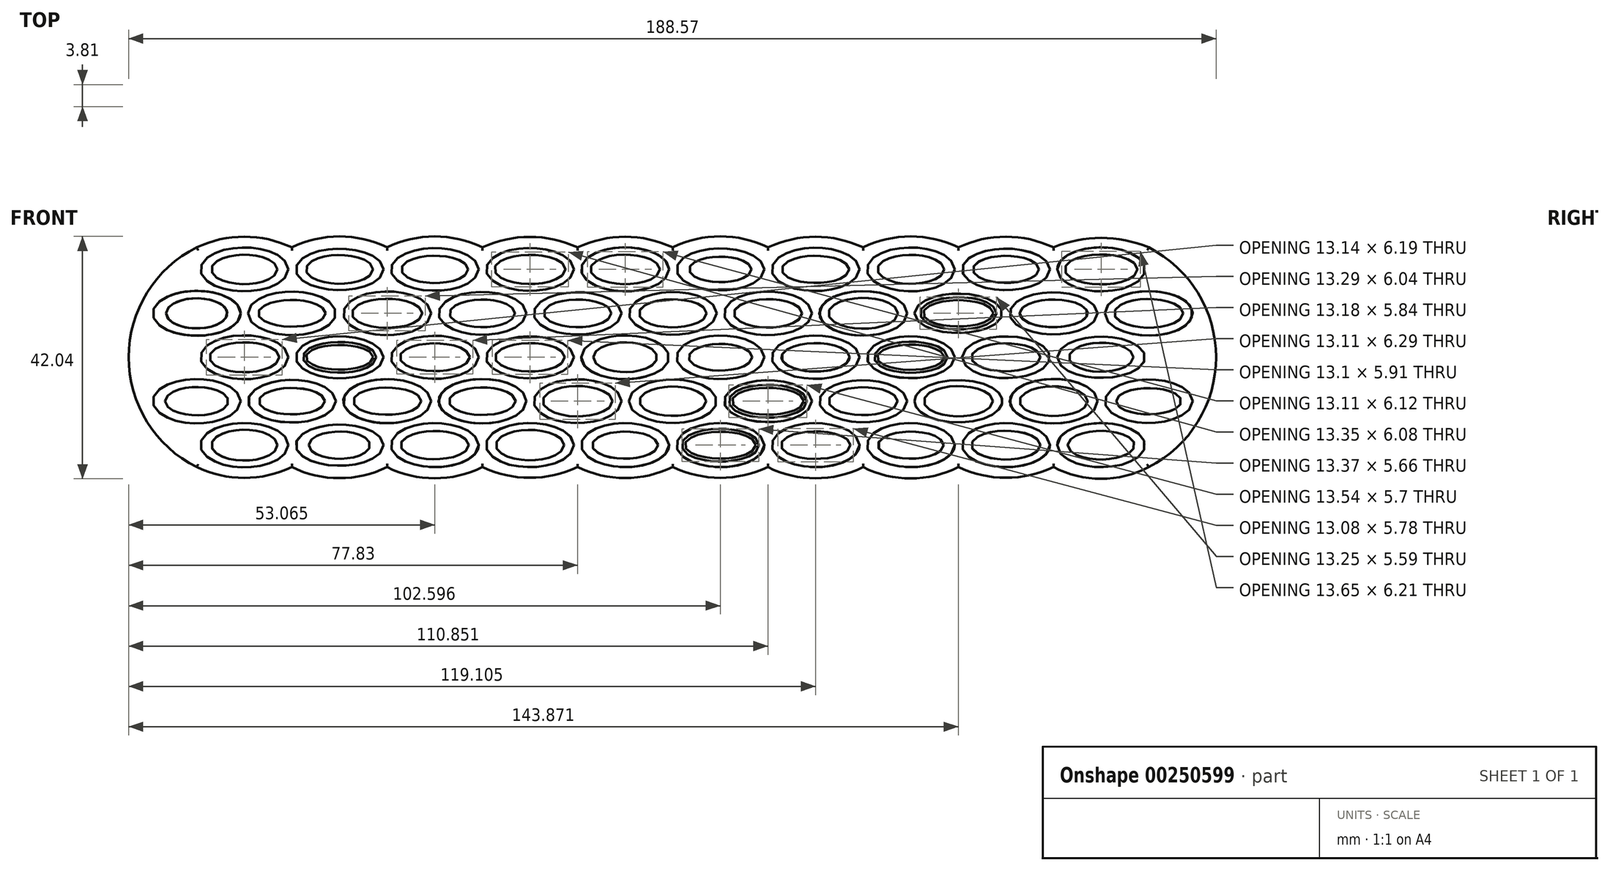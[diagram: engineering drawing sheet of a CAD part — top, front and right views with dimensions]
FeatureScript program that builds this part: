
annotation { "Feature Type Name" : "Feature", "Feature Type Description" : "" }
export const myFeature = defineFeature(function(context is Context, id is Id, definition is map)
    precondition{}
    {
        {
            var Q0;
            Q0=qCreatedBy(makeId("Front.planeOp"),FACE);
            var sketch = newSketch(context, id + "F3", { "sketchPlane" : qUnion([Q0])});
            skPoint(sketch, "E0.middle", {"position": v(0, 0) * mm});
            skEllipse(sketch, "E1", {"center": v(-74.3, 15.24) * mm, "majorRadius": 7.62 * mm, "minorRadius": 3.8 * mm, "majorAxis": v(1, 0)});
            skEllipse(sketch, "E2", {"center": v(-66.04, 7.62) * mm, "majorRadius": 7.62 * mm, "minorRadius": 3.76 * mm, "majorAxis": v(-1, 0)});
            skEllipse(sketch, "E3", {"center": v(-57.79, 15.24) * mm, "majorRadius": 7.62 * mm, "minorRadius": 3.58 * mm, "majorAxis": v(1, 0)});
            skEllipse(sketch, "E4", {"center": v(-66.04, -7.62) * mm, "majorRadius": 7.62 * mm, "minorRadius": 3.7 * mm, "majorAxis": v(1, 0)});
            skEllipse(sketch, "E5", {"center": v(-74.3, -15.24) * mm, "majorRadius": 7.62 * mm, "minorRadius": 3.84 * mm, "majorAxis": v(1, 0)});
            skEllipse(sketch, "E6", {"center": v(-57.79, -15.24) * mm, "majorRadius": 7.62 * mm, "minorRadius": 3.55 * mm, "majorAxis": v(1, 0)});
            skEllipse(sketch, "E7", {"center": v(-74.3, 0) * mm, "majorRadius": 7.62 * mm, "minorRadius": 3.8 * mm, "majorAxis": v(1, 0)});
            skEllipse(sketch, "E8", {"center": v(-57.79, 0) * mm, "majorRadius": 7.62 * mm, "minorRadius": 3.63 * mm, "majorAxis": v(1, 0)});
            skEllipse(sketch, "E9", {"center": v(-49.53, 7.62) * mm, "majorRadius": 7.62 * mm, "minorRadius": 3.79 * mm, "majorAxis": v(1, 0)});
            skEllipse(sketch, "E10", {"center": v(-49.53, -7.62) * mm, "majorRadius": 7.62 * mm, "minorRadius": 3.81 * mm, "majorAxis": v(1, 0)});
            skEllipse(sketch, "E11", {"center": v(-41.28, 15.24) * mm, "majorRadius": 7.62 * mm, "minorRadius": 3.7 * mm, "majorAxis": v(1, 0)});
            skEllipse(sketch, "E12", {"center": v(-41.28, 0) * mm, "majorRadius": 7.62 * mm, "minorRadius": 3.73 * mm, "majorAxis": v(1, 0)});
            skEllipse(sketch, "E13", {"center": v(-41.27, -15.24) * mm, "majorRadius": 7.62 * mm, "minorRadius": 3.81 * mm, "majorAxis": v(1, 0)});
            skEllipse(sketch, "E14", {"center": v(-33.02, 7.62) * mm, "majorRadius": 7.62 * mm, "minorRadius": 3.72 * mm, "majorAxis": v(1, 0)});
            skEllipse(sketch, "E15", {"center": v(-33.02, -7.62) * mm, "majorRadius": 7.62 * mm, "minorRadius": 3.85 * mm, "majorAxis": v(1, 0)});
            skEllipse(sketch, "E16", {"center": v(-24.77, 15.24) * mm, "majorRadius": 7.62 * mm, "minorRadius": 3.72 * mm, "majorAxis": v(1, 0)});
            skEllipse(sketch, "E17", {"center": v(-24.77, 0) * mm, "majorRadius": 7.62 * mm, "minorRadius": 3.64 * mm, "majorAxis": v(1, 0)});
            skEllipse(sketch, "E18", {"center": v(-24.77, -15.24) * mm, "majorRadius": 7.62 * mm, "minorRadius": 3.82 * mm, "majorAxis": v(1, 0)});
            skEllipse(sketch, "E19", {"center": v(-16.51, 7.62) * mm, "majorRadius": 7.62 * mm, "minorRadius": 3.67 * mm, "majorAxis": v(1, 0)});
            skEllipse(sketch, "E20", {"center": v(-16.51, -7.62) * mm, "majorRadius": 7.62 * mm, "minorRadius": 3.8 * mm, "majorAxis": v(1, 0)});
            skEllipse(sketch, "E21", {"center": v(-8.26, 15.24) * mm, "majorRadius": 7.62 * mm, "minorRadius": 3.81 * mm, "majorAxis": v(1, 0)});
            skEllipse(sketch, "E22", {"center": v(-8.25, -15.24) * mm, "majorRadius": 7.62 * mm, "minorRadius": 3.81 * mm, "majorAxis": v(1, 0)});
            skEllipse(sketch, "E23", {"center": v(-8.26, 0) * mm, "majorRadius": 7.62 * mm, "minorRadius": 3.8 * mm, "majorAxis": v(-1, 0)});
            skEllipse(sketch, "E24", {"center": v(0, 7.62) * mm, "majorRadius": 7.62 * mm, "minorRadius": 3.7 * mm, "majorAxis": v(1, 0)});
            skEllipse(sketch, "E25", {"center": v(0, -7.62) * mm, "majorRadius": 7.62 * mm, "minorRadius": 3.77 * mm, "majorAxis": v(-1, 0)});
            skEllipse(sketch, "E26", {"center": v(8.26, 15.24) * mm, "majorRadius": 7.62 * mm, "minorRadius": 3.63 * mm, "majorAxis": v(1, 0)});
            skEllipse(sketch, "E27", {"center": v(8.26, 0) * mm, "majorRadius": 7.62 * mm, "minorRadius": 3.78 * mm, "majorAxis": v(1, 0)});
            skEllipse(sketch, "E28", {"center": v(8.26, -15.24) * mm, "majorRadius": 7.62 * mm, "minorRadius": 3.81 * mm, "majorAxis": v(1, 0)});
            skEllipse(sketch, "E29", {"center": v(16.51, 7.62) * mm, "majorRadius": 7.62 * mm, "minorRadius": 3.79 * mm, "majorAxis": v(1, 0)});
            skEllipse(sketch, "E30", {"center": v(24.77, 15.24) * mm, "majorRadius": 7.62 * mm, "minorRadius": 3.75 * mm, "majorAxis": v(1, 0)});
            skEllipse(sketch, "E31", {"center": v(24.77, 0) * mm, "majorRadius": 7.62 * mm, "minorRadius": 3.75 * mm, "majorAxis": v(1, 0)});
            skEllipse(sketch, "E32", {"center": v(16.51, -7.62) * mm, "majorRadius": 7.62 * mm, "minorRadius": 3.62 * mm, "majorAxis": v(1, 0)});
            skEllipse(sketch, "E33", {"center": v(24.77, -15.24) * mm, "majorRadius": 7.62 * mm, "minorRadius": 3.81 * mm, "majorAxis": v(1, 0)});
            skEllipse(sketch, "E34", {"center": v(33.02, -7.62) * mm, "majorRadius": 7.62 * mm, "minorRadius": 3.65 * mm, "majorAxis": v(1, 0)});
            skEllipse(sketch, "E35", {"center": v(41.28, -15.24) * mm, "majorRadius": 7.62 * mm, "minorRadius": 3.81 * mm, "majorAxis": v(1, 0)});
            skEllipse(sketch, "E36", {"center": v(41.28, 0) * mm, "majorRadius": 7.62 * mm, "minorRadius": 3.62 * mm, "majorAxis": v(1, 0)});
            skEllipse(sketch, "E37", {"center": v(33.02, 7.62) * mm, "majorRadius": 7.62 * mm, "minorRadius": 3.85 * mm, "majorAxis": v(1, 0)});
            skEllipse(sketch, "E38", {"center": v(41.28, 15.24) * mm, "majorRadius": 7.62 * mm, "minorRadius": 3.8 * mm, "majorAxis": v(1, 0)});
            skEllipse(sketch, "E39", {"center": v(49.53, 7.62) * mm, "majorRadius": 7.62 * mm, "minorRadius": 3.41 * mm, "majorAxis": v(-1, 0)});
            skEllipse(sketch, "E40", {"center": v(49.53, -7.62) * mm, "majorRadius": 7.62 * mm, "minorRadius": 3.68 * mm, "majorAxis": v(-1, 0)});
            skEllipse(sketch, "E41", {"center": v(57.79, -15.24) * mm, "majorRadius": 7.62 * mm, "minorRadius": 3.81 * mm, "majorAxis": v(1, 0)});
            skEllipse(sketch, "E42", {"center": v(57.79, 0) * mm, "majorRadius": 7.62 * mm, "minorRadius": 3.6 * mm, "majorAxis": v(-1, 0)});
            skEllipse(sketch, "E43", {"center": v(66.04, 7.62) * mm, "majorRadius": 7.62 * mm, "minorRadius": 3.66 * mm, "majorAxis": v(1, 0)});
            skEllipse(sketch, "E44", {"center": v(57.79, 15.24) * mm, "majorRadius": 7.62 * mm, "minorRadius": 3.6 * mm, "majorAxis": v(1, 0)});
            skPoint(sketch, "E44.centerSnap0", {"position": v(57.79, 3.6) * mm});
            skEllipse(sketch, "E45", {"center": v(66.04, -7.62) * mm, "majorRadius": 7.62 * mm, "minorRadius": 3.85 * mm, "majorAxis": v(1, 0)});
            skEllipse(sketch, "E46", {"center": v(74.3, 15.24) * mm, "majorRadius": 7.62 * mm, "minorRadius": 3.81 * mm, "majorAxis": v(-1, 0)});
            skEllipse(sketch, "E47", {"center": v(74.3, 0) * mm, "majorRadius": 7.62 * mm, "minorRadius": 3.57 * mm, "majorAxis": v(-1, 0)});
            skEllipse(sketch, "E48", {"center": v(74.3, -15.24) * mm, "majorRadius": 7.62 * mm, "minorRadius": 3.81 * mm, "majorAxis": v(-1, 0)});
            skPoint(sketch, "E49.endSnap0", {"position": v(-66.04, 3.86) * mm});
            skArc(sketch, "E50", {"start": v(-66.04, 19.05) * mm, "mid": v(-74.3, 20.91) * mm, "end": v(-82.55, 19.05) * mm});
            skArc(sketch, "E51", {"start": v(-49.53, 19.05) * mm, "mid": v(-57.79, 20.96) * mm, "end": v(-66.04, 19.05) * mm});
            skArc(sketch, "E52", {"start": v(-33.02, 19.05) * mm, "mid": v(-41.28, 20.96) * mm, "end": v(-49.53, 19.05) * mm});
            skArc(sketch, "E53", {"start": v(-16.51, 19.05) * mm, "mid": v(-24.77, 20.88) * mm, "end": v(-33.02, 19.05) * mm});
            skArc(sketch, "E54", {"start": v(0, 19.05) * mm, "mid": v(-8.26, 20.9) * mm, "end": v(-16.51, 19.05) * mm});
            skArc(sketch, "E55", {"start": v(16.51, 19.05) * mm, "mid": v(8.26, 20.97) * mm, "end": v(0, 19.05) * mm});
            skArc(sketch, "E56", {"start": v(33.02, 19.05) * mm, "mid": v(24.77, 20.9) * mm, "end": v(16.51, 19.05) * mm});
            skArc(sketch, "E57", {"start": v(49.53, 19.05) * mm, "mid": v(41.28, 20.96) * mm, "end": v(33.02, 19.05) * mm});
            skArc(sketch, "E58", {"start": v(66.04, 19.05) * mm, "mid": v(57.79, 20.9) * mm, "end": v(49.53, 19.05) * mm});
            skArc(sketch, "E59", {"start": v(82.55, 19.05) * mm, "mid": v(74.3, 20.7) * mm, "end": v(66.04, 19.05) * mm});
            skPoint(sketch, "E60.endSnap0", {"position": v(81.92, 0) * mm});
            skArc(sketch, "E61", {"start": v(-82.55, -19.05) * mm, "mid": v(-74.3, -20.92) * mm, "end": v(-66.04, -19.05) * mm});
            skArc(sketch, "E62", {"start": v(-66.04, -19.05) * mm, "mid": v(-57.79, -20.96) * mm, "end": v(-49.53, -19.05) * mm});
            skArc(sketch, "E63", {"start": v(-49.53, -19.05) * mm, "mid": v(-41.28, -20.99) * mm, "end": v(-33.02, -19.05) * mm});
            skArc(sketch, "E64", {"start": v(-33.02, -19.05) * mm, "mid": v(-24.77, -20.9) * mm, "end": v(-16.51, -19.05) * mm});
            skArc(sketch, "E65", {"start": v(-16.5, -19.05) * mm, "mid": v(-8.25, -20.94) * mm, "end": v(0, -19.05) * mm});
            skArc(sketch, "E66", {"start": v(0, -19.05) * mm, "mid": v(8.26, -20.9) * mm, "end": v(16.51, -19.05) * mm});
            skArc(sketch, "E67", {"start": v(16.51, -19.05) * mm, "mid": v(24.77, -21) * mm, "end": v(33.02, -19.05) * mm});
            skArc(sketch, "E68", {"start": v(33.02, -19.05) * mm, "mid": v(41.28, -21.02) * mm, "end": v(49.53, -19.05) * mm});
            skArc(sketch, "E69", {"start": v(49.53, -19.05) * mm, "mid": v(57.79, -20.9) * mm, "end": v(66.04, -19.05) * mm});
            skArc(sketch, "E70", {"start": v(66.04, -19.05) * mm, "mid": v(74.3, -21.07) * mm, "end": v(82.55, -19.05) * mm});
            skArc(sketch, "E71", {"start": v(82.55, -19.05) * mm, "mid": v(94.23, 0) * mm, "end": v(82.55, 19.05) * mm});
            skPoint(sketch, "E72.endSnap0", {"position": v(73.66, -7.62) * mm});
            skEllipse(sketch, "E73", {"center": v(82.55, 7.62) * mm, "majorRadius": 7.62 * mm, "minorRadius": 3.85 * mm, "majorAxis": v(-1, 0)});
            skEllipse(sketch, "E74", {"center": v(82.55, -7.62) * mm, "majorRadius": 7.62 * mm, "minorRadius": 3.76 * mm, "majorAxis": v(1, 0)});
            skArc(sketch, "E75", {"start": v(-82.55, 19.05) * mm, "mid": v(-94.34, 0) * mm, "end": v(-82.55, -19.05) * mm});
            skEllipse(sketch, "E76", {"center": v(-82.55, 7.62) * mm, "majorRadius": 7.62 * mm, "minorRadius": 3.88 * mm, "majorAxis": v(1, 0)});
            skPoint(sketch, "E76.centerSnap0", {"position": v(-77.03, 7.62) * mm});
            skEllipse(sketch, "E77", {"center": v(-82.55, -7.62) * mm, "majorRadius": 7.62 * mm, "minorRadius": 3.83 * mm, "majorAxis": v(1, 0)});
            skEllipse(sketch, "E78", {"center": v(74.3, 15.24) * mm, "majorRadius": 6.32 * mm, "minorRadius": 2.6 * mm, "majorAxis": v(1, 0)});
            skEllipse(sketch, "E79", {"center": v(82.55, 7.62) * mm, "majorRadius": 5.98 * mm, "minorRadius": 2.5 * mm, "majorAxis": v(1, 0)});
            skEllipse(sketch, "E80", {"center": v(74.3, 0) * mm, "majorRadius": 5.58 * mm, "minorRadius": 2.51 * mm, "majorAxis": v(1, 0)});
            skEllipse(sketch, "E81", {"center": v(82.55, -7.62) * mm, "majorRadius": 5.66 * mm, "minorRadius": 2.27 * mm, "majorAxis": v(-1, 0)});
            skEllipse(sketch, "E82", {"center": v(57.79, 15.24) * mm, "majorRadius": 5.74 * mm, "minorRadius": 2.35 * mm, "majorAxis": v(1, 0)});
            skEllipse(sketch, "E83", {"center": v(66.04, 7.62) * mm, "majorRadius": 5.9 * mm, "minorRadius": 2.38 * mm, "majorAxis": v(-1, 0)});
            skEllipse(sketch, "E84", {"center": v(74.3, -15.24) * mm, "majorRadius": 5.8 * mm, "minorRadius": 2.49 * mm, "majorAxis": v(-1, 0)});
            skEllipse(sketch, "E85", {"center": v(66.04, -7.62) * mm, "majorRadius": 5.93 * mm, "minorRadius": 2.57 * mm, "majorAxis": v(1, 0)});
            skEllipse(sketch, "E86", {"center": v(57.79, -15.24) * mm, "majorRadius": 5.97 * mm, "minorRadius": 2.5 * mm, "majorAxis": v(1, 0)});
            skEllipse(sketch, "E87", {"center": v(57.79, 0) * mm, "majorRadius": 6 * mm, "minorRadius": 2.43 * mm, "majorAxis": v(1, 0)});
            skEllipse(sketch, "E88", {"center": v(49.53, 7.62) * mm, "majorRadius": 6.12 * mm, "minorRadius": 2.29 * mm, "majorAxis": v(1, 0)});
            skEllipse(sketch, "E89", {"center": v(41.28, 15.24) * mm, "majorRadius": 5.78 * mm, "minorRadius": 2.5 * mm, "majorAxis": v(1, 0)});
            skEllipse(sketch, "E90", {"center": v(33.02, 7.62) * mm, "majorRadius": 6.02 * mm, "minorRadius": 2.67 * mm, "majorAxis": v(1, 0)});
            skEllipse(sketch, "E91", {"center": v(24.77, 15.24) * mm, "majorRadius": 5.85 * mm, "minorRadius": 2.36 * mm, "majorAxis": v(1, 0)});
            skEllipse(sketch, "E92", {"center": v(8.26, 15.24) * mm, "majorRadius": 5.43 * mm, "minorRadius": 2.2 * mm, "majorAxis": v(1, 0)});
            skEllipse(sketch, "E93", {"center": v(16.51, 7.62) * mm, "majorRadius": 5.93 * mm, "minorRadius": 2.46 * mm, "majorAxis": v(1, 0)});
            skEllipse(sketch, "E94", {"center": v(24.77, 0) * mm, "majorRadius": 5.93 * mm, "minorRadius": 2.47 * mm, "majorAxis": v(1, 0)});
            skEllipse(sketch, "E95", {"center": v(41.28, 0) * mm, "majorRadius": 5.84 * mm, "minorRadius": 2.19 * mm, "majorAxis": v(1, 0)});
            skEllipse(sketch, "E96", {"center": v(49.53, -7.62) * mm, "majorRadius": 5.98 * mm, "minorRadius": 2.63 * mm, "majorAxis": v(1, 0)});
            skEllipse(sketch, "E97", {"center": v(33.02, -7.62) * mm, "majorRadius": 6 * mm, "minorRadius": 2.41 * mm, "majorAxis": v(1, 0)});
            skEllipse(sketch, "E98", {"center": v(41.28, -15.24) * mm, "majorRadius": 5.7 * mm, "minorRadius": 2.35 * mm, "majorAxis": v(1, 0)});
            skEllipse(sketch, "E99", {"center": v(24.77, -15.24) * mm, "majorRadius": 6.03 * mm, "minorRadius": 2.38 * mm, "majorAxis": v(1, 0)});
            skEllipse(sketch, "E100", {"center": v(16.51, -7.62) * mm, "majorRadius": 6.26 * mm, "minorRadius": 2.34 * mm, "majorAxis": v(1, 0)});
            skEllipse(sketch, "E101", {"center": v(8.26, -15.24) * mm, "majorRadius": 6.18 * mm, "minorRadius": 2.32 * mm, "majorAxis": v(1, 0)});
            skEllipse(sketch, "E102", {"center": v(0, 7.62) * mm, "majorRadius": 5.88 * mm, "minorRadius": 2.43 * mm, "majorAxis": v(1, 0)});
            skEllipse(sketch, "E103", {"center": v(8.26, 0) * mm, "majorRadius": 5.5 * mm, "minorRadius": 2.3 * mm, "majorAxis": v(1, 0)});
            skEllipse(sketch, "E104", {"center": v(0, -7.62) * mm, "majorRadius": 5.79 * mm, "minorRadius": 2.54 * mm, "majorAxis": v(1, 0)});
            skEllipse(sketch, "E105", {"center": v(-8.26, 0) * mm, "majorRadius": 5.54 * mm, "minorRadius": 2.57 * mm, "majorAxis": v(-1, 0)});
            skEllipse(sketch, "E106", {"center": v(-24.77, 15.24) * mm, "majorRadius": 6.16 * mm, "minorRadius": 2.53 * mm, "majorAxis": v(1, 0)});
            skEllipse(sketch, "E107", {"center": v(-8.26, 15.24) * mm, "majorRadius": 6.05 * mm, "minorRadius": 2.55 * mm, "majorAxis": v(1, 0)});
            skEllipse(sketch, "E108", {"center": v(-16.51, 7.62) * mm, "majorRadius": 5.88 * mm, "minorRadius": 2.4 * mm, "majorAxis": v(1, 0)});
            skEllipse(sketch, "E109", {"center": v(-41.28, 15.24) * mm, "majorRadius": 5.8 * mm, "minorRadius": 2.37 * mm, "majorAxis": v(1, 0)});
            skEllipse(sketch, "E110", {"center": v(-33.02, 7.62) * mm, "majorRadius": 5.7 * mm, "minorRadius": 2.39 * mm, "majorAxis": v(1, 0)});
            skEllipse(sketch, "E111", {"center": v(-24.77, 0) * mm, "majorRadius": 6.04 * mm, "minorRadius": 2.45 * mm, "majorAxis": v(1, 0)});
            skEllipse(sketch, "E112", {"center": v(-16.51, -7.62) * mm, "majorRadius": 6.05 * mm, "minorRadius": 2.64 * mm, "majorAxis": v(1, 0)});
            skEllipse(sketch, "E113", {"center": v(-8.25, -15.24) * mm, "majorRadius": 5.72 * mm, "minorRadius": 2.35 * mm, "majorAxis": v(1, 0)});
            skEllipse(sketch, "E114", {"center": v(-24.77, -15.24) * mm, "majorRadius": 5.94 * mm, "minorRadius": 2.63 * mm, "majorAxis": v(1, 0)});
            skEllipse(sketch, "E115", {"center": v(-41.27, -15.24) * mm, "majorRadius": 5.92 * mm, "minorRadius": 2.44 * mm, "majorAxis": v(1, 0)});
            skEllipse(sketch, "E116", {"center": v(-33.02, -7.62) * mm, "majorRadius": 5.8 * mm, "minorRadius": 2.38 * mm, "majorAxis": v(1, 0)});
            skEllipse(sketch, "E117", {"center": v(-41.28, 0) * mm, "majorRadius": 6.08 * mm, "minorRadius": 2.41 * mm, "majorAxis": v(1, 0)});
            skEllipse(sketch, "E118", {"center": v(-49.53, 7.62) * mm, "majorRadius": 6.14 * mm, "minorRadius": 2.51 * mm, "majorAxis": v(1, 0)});
            skEllipse(sketch, "E119", {"center": v(-57.79, 15.24) * mm, "majorRadius": 5.81 * mm, "minorRadius": 2.5 * mm, "majorAxis": v(1, 0)});
            skEllipse(sketch, "E120", {"center": v(-66.04, 7.62) * mm, "majorRadius": 5.84 * mm, "minorRadius": 2.32 * mm, "majorAxis": v(1, 0)});
            skEllipse(sketch, "E121", {"center": v(-74.3, 15.24) * mm, "majorRadius": 5.74 * mm, "minorRadius": 2.55 * mm, "majorAxis": v(1, 0)});
            skEllipse(sketch, "E122", {"center": v(-82.55, 7.62) * mm, "majorRadius": 5.32 * mm, "minorRadius": 2.6 * mm, "majorAxis": v(-1, 0)});
            skEllipse(sketch, "E123", {"center": v(-74.3, 0) * mm, "majorRadius": 6.06 * mm, "minorRadius": 2.58 * mm, "majorAxis": v(1, 0)});
            skEllipse(sketch, "E124", {"center": v(-82.55, -7.62) * mm, "majorRadius": 5.5 * mm, "minorRadius": 2.44 * mm, "majorAxis": v(-1, 0)});
            skEllipse(sketch, "E125", {"center": v(-74.3, -15.24) * mm, "majorRadius": 5.74 * mm, "minorRadius": 2.68 * mm, "majorAxis": v(1, 0)});
            skEllipse(sketch, "E126", {"center": v(-57.79, -15.24) * mm, "majorRadius": 5.3 * mm, "minorRadius": 2.37 * mm, "majorAxis": v(-1, 0)});
            skEllipse(sketch, "E127", {"center": v(-66.04, -7.62) * mm, "majorRadius": 5.74 * mm, "minorRadius": 2.3 * mm, "majorAxis": v(1, 0)});
            skEllipse(sketch, "E128", {"center": v(-57.79, 0) * mm, "majorRadius": 5.85 * mm, "minorRadius": 2.13 * mm, "majorAxis": v(1, 0)});
            skEllipse(sketch, "E129", {"center": v(-49.53, -7.62) * mm, "majorRadius": 5.9 * mm, "minorRadius": 2.36 * mm, "majorAxis": v(1, 0)});
            skSolve(sketch);
        }
        {
            var Q0;
            Q0=makeQuery(id+"F3.imprint","IMPRINT",FACE,{"disambiguationData":[TD([[makeQuery(id+"F3.imprint","IMPRINT",EDGE,{"derivedFrom":sQuery(id+"F3.wireOp",EDGE,"E1")}),-1.0]])]});
            extrude(context, id + "F0", {"entities" : qUnion([Q0]), "depth" : 2.54 * mm});
        }
        {
            var Q0;
            Q0=makeQuery(id+"F3.imprint","IMPRINT",FACE,{"disambiguationData":[TD([[makeQuery(id+"F3.imprint","IMPRINT",EDGE,{"derivedFrom":sQuery(id+"F3.wireOp",EDGE,"E1")}),1.0]])]});
            var Q1;
            Q1=makeQuery(id+"F3.imprint","IMPRINT",FACE,{"disambiguationData":[TD([[makeQuery(id+"F3.imprint","IMPRINT",EDGE,{"derivedFrom":sQuery(id+"F3.wireOp",EDGE,"E76")}),1.0]])]});
            var Q2;
            Q2=makeQuery(id+"F3.imprint","IMPRINT",FACE,{"disambiguationData":[TD([[makeQuery(id+"F3.imprint","IMPRINT",EDGE,{"derivedFrom":sQuery(id+"F3.wireOp",EDGE,"E7")}),1.0]])]});
            var Q3;
            Q3=makeQuery(id+"F3.imprint","IMPRINT",FACE,{"disambiguationData":[TD([[makeQuery(id+"F3.imprint","IMPRINT",EDGE,{"derivedFrom":sQuery(id+"F3.wireOp",EDGE,"E77")}),1.0]])]});
            var Q4;
            Q4=makeQuery(id+"F3.imprint","IMPRINT",FACE,{"disambiguationData":[TD([[makeQuery(id+"F3.imprint","IMPRINT",EDGE,{"derivedFrom":sQuery(id+"F3.wireOp",EDGE,"E5")}),1.0]])]});
            var Q5;
            Q5=makeQuery(id+"F3.imprint","IMPRINT",FACE,{"disambiguationData":[TD([[makeQuery(id+"F3.imprint","IMPRINT",EDGE,{"derivedFrom":sQuery(id+"F3.wireOp",EDGE,"E4")}),1.0]])]});
            var Q6;
            Q6=makeQuery(id+"F3.imprint","IMPRINT",FACE,{"disambiguationData":[TD([[makeQuery(id+"F3.imprint","IMPRINT",EDGE,{"derivedFrom":sQuery(id+"F3.wireOp",EDGE,"E6")}),1.0]])]});
            var Q7;
            Q7=makeQuery(id+"F3.imprint","IMPRINT",FACE,{"disambiguationData":[TD([[makeQuery(id+"F3.imprint","IMPRINT",EDGE,{"derivedFrom":sQuery(id+"F3.wireOp",EDGE,"E10")}),1.0]])]});
            var Q8;
            Q8=makeQuery(id+"F3.imprint","IMPRINT",FACE,{"disambiguationData":[TD([[makeQuery(id+"F3.imprint","IMPRINT",EDGE,{"derivedFrom":sQuery(id+"F3.wireOp",EDGE,"E8")}),1.0]])]});
            var Q9;
            Q9=makeQuery(id+"F3.imprint","IMPRINT",FACE,{"disambiguationData":[TD([[makeQuery(id+"F3.imprint","IMPRINT",EDGE,{"derivedFrom":sQuery(id+"F3.wireOp",EDGE,"E2")}),1.0]])]});
            var Q10;
            Q10=makeQuery(id+"F3.imprint","IMPRINT",FACE,{"disambiguationData":[TD([[makeQuery(id+"F3.imprint","IMPRINT",EDGE,{"derivedFrom":sQuery(id+"F3.wireOp",EDGE,"E3")}),1.0]])]});
            var Q11;
            Q11=makeQuery(id+"F3.imprint","IMPRINT",FACE,{"disambiguationData":[TD([[makeQuery(id+"F3.imprint","IMPRINT",EDGE,{"derivedFrom":sQuery(id+"F3.wireOp",EDGE,"E9")}),1.0]])]});
            var Q12;
            Q12=makeQuery(id+"F3.imprint","IMPRINT",FACE,{"disambiguationData":[TD([[makeQuery(id+"F3.imprint","IMPRINT",EDGE,{"derivedFrom":sQuery(id+"F3.wireOp",EDGE,"E11")}),1.0]])]});
            var Q13;
            Q13=makeQuery(id+"F3.imprint","IMPRINT",FACE,{"disambiguationData":[TD([[makeQuery(id+"F3.imprint","IMPRINT",EDGE,{"derivedFrom":sQuery(id+"F3.wireOp",EDGE,"E13")}),1.0]])]});
            var Q14;
            Q14=makeQuery(id+"F3.imprint","IMPRINT",FACE,{"disambiguationData":[TD([[makeQuery(id+"F3.imprint","IMPRINT",EDGE,{"derivedFrom":sQuery(id+"F3.wireOp",EDGE,"E15")}),1.0]])]});
            var Q15;
            Q15=makeQuery(id+"F3.imprint","IMPRINT",FACE,{"disambiguationData":[TD([[makeQuery(id+"F3.imprint","IMPRINT",EDGE,{"derivedFrom":sQuery(id+"F3.wireOp",EDGE,"E12")}),1.0]])]});
            var Q16;
            Q16=makeQuery(id+"F3.imprint","IMPRINT",FACE,{"disambiguationData":[TD([[makeQuery(id+"F3.imprint","IMPRINT",EDGE,{"derivedFrom":sQuery(id+"F3.wireOp",EDGE,"E14")}),1.0]])]});
            var Q17;
            Q17=makeQuery(id+"F3.imprint","IMPRINT",FACE,{"disambiguationData":[TD([[makeQuery(id+"F3.imprint","IMPRINT",EDGE,{"derivedFrom":sQuery(id+"F3.wireOp",EDGE,"E16")}),1.0]])]});
            var Q18;
            Q18=makeQuery(id+"F3.imprint","IMPRINT",FACE,{"disambiguationData":[TD([[makeQuery(id+"F3.imprint","IMPRINT",EDGE,{"derivedFrom":sQuery(id+"F3.wireOp",EDGE,"E17")}),1.0]])]});
            var Q19;
            Q19=makeQuery(id+"F3.imprint","IMPRINT",FACE,{"disambiguationData":[TD([[makeQuery(id+"F3.imprint","IMPRINT",EDGE,{"derivedFrom":sQuery(id+"F3.wireOp",EDGE,"E19")}),1.0]])]});
            var Q20;
            Q20=makeQuery(id+"F3.imprint","IMPRINT",FACE,{"disambiguationData":[TD([[makeQuery(id+"F3.imprint","IMPRINT",EDGE,{"derivedFrom":sQuery(id+"F3.wireOp",EDGE,"E21")}),1.0]])]});
            var Q21;
            Q21=makeQuery(id+"F3.imprint","IMPRINT",FACE,{"disambiguationData":[TD([[makeQuery(id+"F3.imprint","IMPRINT",EDGE,{"derivedFrom":sQuery(id+"F3.wireOp",EDGE,"E20")}),1.0]])]});
            var Q22;
            Q22=makeQuery(id+"F3.imprint","IMPRINT",FACE,{"disambiguationData":[TD([[makeQuery(id+"F3.imprint","IMPRINT",EDGE,{"derivedFrom":sQuery(id+"F3.wireOp",EDGE,"E23")}),1.0]])]});
            var Q23;
            Q23=makeQuery(id+"F3.imprint","IMPRINT",FACE,{"disambiguationData":[TD([[makeQuery(id+"F3.imprint","IMPRINT",EDGE,{"derivedFrom":sQuery(id+"F3.wireOp",EDGE,"E18")}),1.0]])]});
            var Q24;
            Q24=makeQuery(id+"F3.imprint","IMPRINT",FACE,{"disambiguationData":[TD([[makeQuery(id+"F3.imprint","IMPRINT",EDGE,{"derivedFrom":sQuery(id+"F3.wireOp",EDGE,"E24")}),1.0]])]});
            var Q25;
            Q25=makeQuery(id+"F3.imprint","IMPRINT",FACE,{"disambiguationData":[TD([[makeQuery(id+"F3.imprint","IMPRINT",EDGE,{"derivedFrom":sQuery(id+"F3.wireOp",EDGE,"E22")}),1.0]])]});
            var Q26;
            Q26=makeQuery(id+"F3.imprint","IMPRINT",FACE,{"disambiguationData":[TD([[makeQuery(id+"F3.imprint","IMPRINT",EDGE,{"derivedFrom":sQuery(id+"F3.wireOp",EDGE,"E25")}),1.0]])]});
            var Q27;
            Q27=makeQuery(id+"F3.imprint","IMPRINT",FACE,{"disambiguationData":[TD([[makeQuery(id+"F3.imprint","IMPRINT",EDGE,{"derivedFrom":sQuery(id+"F3.wireOp",EDGE,"E28")}),1.0]])]});
            var Q28;
            Q28=makeQuery(id+"F3.imprint","IMPRINT",FACE,{"disambiguationData":[TD([[makeQuery(id+"F3.imprint","IMPRINT",EDGE,{"derivedFrom":sQuery(id+"F3.wireOp",EDGE,"E32")}),1.0]])]});
            var Q29;
            Q29=makeQuery(id+"F3.imprint","IMPRINT",FACE,{"disambiguationData":[TD([[makeQuery(id+"F3.imprint","IMPRINT",EDGE,{"derivedFrom":sQuery(id+"F3.wireOp",EDGE,"E27")}),1.0]])]});
            var Q30;
            Q30=makeQuery(id+"F3.imprint","IMPRINT",FACE,{"disambiguationData":[TD([[makeQuery(id+"F3.imprint","IMPRINT",EDGE,{"derivedFrom":sQuery(id+"F3.wireOp",EDGE,"E29")}),1.0]])]});
            var Q31;
            Q31=makeQuery(id+"F3.imprint","IMPRINT",FACE,{"disambiguationData":[TD([[makeQuery(id+"F3.imprint","IMPRINT",EDGE,{"derivedFrom":sQuery(id+"F3.wireOp",EDGE,"E26")}),1.0]])]});
            var Q32;
            Q32=makeQuery(id+"F3.imprint","IMPRINT",FACE,{"disambiguationData":[TD([[makeQuery(id+"F3.imprint","IMPRINT",EDGE,{"derivedFrom":sQuery(id+"F3.wireOp",EDGE,"E30")}),1.0]])]});
            var Q33;
            Q33=makeQuery(id+"F3.imprint","IMPRINT",FACE,{"disambiguationData":[TD([[makeQuery(id+"F3.imprint","IMPRINT",EDGE,{"derivedFrom":sQuery(id+"F3.wireOp",EDGE,"E33")}),1.0]])]});
            var Q34;
            Q34=makeQuery(id+"F3.imprint","IMPRINT",FACE,{"disambiguationData":[TD([[makeQuery(id+"F3.imprint","IMPRINT",EDGE,{"derivedFrom":sQuery(id+"F3.wireOp",EDGE,"E31")}),1.0]])]});
            var Q35;
            Q35=makeQuery(id+"F3.imprint","IMPRINT",FACE,{"disambiguationData":[TD([[makeQuery(id+"F3.imprint","IMPRINT",EDGE,{"derivedFrom":sQuery(id+"F3.wireOp",EDGE,"E34")}),1.0]])]});
            var Q36;
            Q36=makeQuery(id+"F3.imprint","IMPRINT",FACE,{"disambiguationData":[TD([[makeQuery(id+"F3.imprint","IMPRINT",EDGE,{"derivedFrom":sQuery(id+"F3.wireOp",EDGE,"E37")}),1.0]])]});
            var Q37;
            Q37=makeQuery(id+"F3.imprint","IMPRINT",FACE,{"disambiguationData":[TD([[makeQuery(id+"F3.imprint","IMPRINT",EDGE,{"derivedFrom":sQuery(id+"F3.wireOp",EDGE,"E35")}),1.0]])]});
            var Q38;
            Q38=makeQuery(id+"F3.imprint","IMPRINT",FACE,{"disambiguationData":[TD([[makeQuery(id+"F3.imprint","IMPRINT",EDGE,{"derivedFrom":sQuery(id+"F3.wireOp",EDGE,"E40")}),1.0]])]});
            var Q39;
            Q39=makeQuery(id+"F3.imprint","IMPRINT",FACE,{"disambiguationData":[TD([[makeQuery(id+"F3.imprint","IMPRINT",EDGE,{"derivedFrom":sQuery(id+"F3.wireOp",EDGE,"E36")}),1.0]])]});
            var Q40;
            Q40=makeQuery(id+"F3.imprint","IMPRINT",FACE,{"disambiguationData":[TD([[makeQuery(id+"F3.imprint","IMPRINT",EDGE,{"derivedFrom":sQuery(id+"F3.wireOp",EDGE,"E38")}),1.0]])]});
            var Q41;
            Q41=makeQuery(id+"F3.imprint","IMPRINT",FACE,{"disambiguationData":[TD([[makeQuery(id+"F3.imprint","IMPRINT",EDGE,{"derivedFrom":sQuery(id+"F3.wireOp",EDGE,"E39")}),1.0]])]});
            var Q42;
            Q42=makeQuery(id+"F3.imprint","IMPRINT",FACE,{"disambiguationData":[TD([[makeQuery(id+"F3.imprint","IMPRINT",EDGE,{"derivedFrom":sQuery(id+"F3.wireOp",EDGE,"E41")}),1.0]])]});
            var Q43;
            Q43=makeQuery(id+"F3.imprint","IMPRINT",FACE,{"disambiguationData":[TD([[makeQuery(id+"F3.imprint","IMPRINT",EDGE,{"derivedFrom":sQuery(id+"F3.wireOp",EDGE,"E45")}),1.0]])]});
            var Q44;
            Q44=makeQuery(id+"F3.imprint","IMPRINT",FACE,{"disambiguationData":[TD([[makeQuery(id+"F3.imprint","IMPRINT",EDGE,{"derivedFrom":sQuery(id+"F3.wireOp",EDGE,"E42")}),1.0]])]});
            var Q45;
            Q45=makeQuery(id+"F3.imprint","IMPRINT",FACE,{"disambiguationData":[TD([[makeQuery(id+"F3.imprint","IMPRINT",EDGE,{"derivedFrom":sQuery(id+"F3.wireOp",EDGE,"E43")}),1.0]])]});
            var Q46;
            Q46=makeQuery(id+"F3.imprint","IMPRINT",FACE,{"disambiguationData":[TD([[makeQuery(id+"F3.imprint","IMPRINT",EDGE,{"derivedFrom":sQuery(id+"F3.wireOp",EDGE,"E44")}),1.0]])]});
            var Q47;
            Q47=makeQuery(id+"F3.imprint","IMPRINT",FACE,{"disambiguationData":[TD([[makeQuery(id+"F3.imprint","IMPRINT",EDGE,{"derivedFrom":sQuery(id+"F3.wireOp",EDGE,"E48")}),1.0]])]});
            var Q48;
            Q48=makeQuery(id+"F3.imprint","IMPRINT",FACE,{"disambiguationData":[TD([[makeQuery(id+"F3.imprint","IMPRINT",EDGE,{"derivedFrom":sQuery(id+"F3.wireOp",EDGE,"E74")}),1.0]])]});
            var Q49;
            Q49=makeQuery(id+"F3.imprint","IMPRINT",FACE,{"disambiguationData":[TD([[makeQuery(id+"F3.imprint","IMPRINT",EDGE,{"derivedFrom":sQuery(id+"F3.wireOp",EDGE,"E47")}),1.0]])]});
            var Q50;
            Q50=makeQuery(id+"F3.imprint","IMPRINT",FACE,{"disambiguationData":[TD([[makeQuery(id+"F3.imprint","IMPRINT",EDGE,{"derivedFrom":sQuery(id+"F3.wireOp",EDGE,"E73")}),1.0]])]});
            var Q51;
            Q51=makeQuery(id+"F3.imprint","IMPRINT",FACE,{"disambiguationData":[TD([[makeQuery(id+"F3.imprint","IMPRINT",EDGE,{"derivedFrom":sQuery(id+"F3.wireOp",EDGE,"E46")}),1.0]])]});
            extrude(context, id + "F1", {"entities" : qUnion([Q0, Q1, Q2, Q3, Q4, Q5, Q6, Q7, Q8, Q9, Q10, Q11, Q12, Q13, Q14, Q15, Q16, Q17, Q18, Q19, Q20, Q21, Q22, Q23, Q24, Q25, Q26, Q27, Q28, Q29, Q30, Q31, Q32, Q33, Q34, Q35, Q36, Q37, Q38, Q39, Q40, Q41, Q42, Q43, Q44, Q45, Q46, Q47, Q48, Q49, Q50, Q51]), "operationType" : NewBodyOperationType.ADD, "depth" : 3.8 * mm});
        }
        {
            var Q0;
            Q0=makeQuery(id+"F1.opExtrude","CAP_EDGE",EDGE,{"disambiguationData":[OSD([sQuery(id+"F3.wireOp",EDGE,"E1")])],"isStart":false});
            var Q1;
            Q1=makeQuery(id+"F1.opExtrude","CAP_EDGE",EDGE,{"disambiguationData":[OSD([sQuery(id+"F3.wireOp",EDGE,"E121")])],"isStart":false});
            var Q2;
            Q2=makeQuery(id+"F1.opExtrude","CAP_EDGE",EDGE,{"disambiguationData":[OSD([sQuery(id+"F3.wireOp",EDGE,"E122")])],"isStart":false});
            var Q3;
            Q3=makeQuery(id+"F1.opExtrude","CAP_EDGE",EDGE,{"disambiguationData":[OSD([sQuery(id+"F3.wireOp",EDGE,"E76")])],"isStart":false});
            var Q4;
            Q4=makeQuery(id+"F1.opExtrude","CAP_EDGE",EDGE,{"disambiguationData":[OSD([sQuery(id+"F3.wireOp",EDGE,"E123")])],"isStart":false});
            var Q5;
            Q5=makeQuery(id+"F1.opExtrude","CAP_EDGE",EDGE,{"disambiguationData":[OSD([sQuery(id+"F3.wireOp",EDGE,"E7")])],"isStart":false});
            var Q6;
            Q6=makeQuery(id+"F1.opExtrude","CAP_EDGE",EDGE,{"disambiguationData":[OSD([sQuery(id+"F3.wireOp",EDGE,"E77")])],"isStart":false});
            var Q7;
            Q7=makeQuery(id+"F1.opExtrude","CAP_EDGE",EDGE,{"disambiguationData":[OSD([sQuery(id+"F3.wireOp",EDGE,"E124")])],"isStart":false});
            var Q8;
            Q8=makeQuery(id+"F1.opExtrude","CAP_EDGE",EDGE,{"disambiguationData":[OSD([sQuery(id+"F3.wireOp",EDGE,"E125")])],"isStart":false});
            var Q9;
            Q9=makeQuery(id+"F1.opExtrude","CAP_EDGE",EDGE,{"disambiguationData":[OSD([sQuery(id+"F3.wireOp",EDGE,"E5")])],"isStart":false});
            var Q10;
            Q10=makeQuery(id+"F1.opExtrude","CAP_EDGE",EDGE,{"disambiguationData":[OSD([sQuery(id+"F3.wireOp",EDGE,"E4")])],"isStart":false});
            var Q11;
            Q11=makeQuery(id+"F1.opExtrude","CAP_EDGE",EDGE,{"disambiguationData":[OSD([sQuery(id+"F3.wireOp",EDGE,"E127")])],"isStart":false});
            var Q12;
            Q12=makeQuery(id+"F1.opExtrude","CAP_EDGE",EDGE,{"disambiguationData":[OSD([sQuery(id+"F3.wireOp",EDGE,"E8")])],"isStart":false});
            var Q13;
            Q13=makeQuery(id+"F1.opExtrude","CAP_EDGE",EDGE,{"disambiguationData":[OSD([sQuery(id+"F3.wireOp",EDGE,"E128")])],"isStart":false});
            var Q14;
            Q14=makeQuery(id+"F0.opExtrude","CAP_EDGE",EDGE,{"disambiguationData":[OSD([sQuery(id+"F3.wireOp",EDGE,"E2")])],"isStart":false});
            var Q15;
            Q15=makeQuery(id+"F1.opExtrude","CAP_EDGE",EDGE,{"disambiguationData":[OSD([sQuery(id+"F3.wireOp",EDGE,"E120")])],"isStart":false});
            var Q16;
            Q16=makeQuery(id+"F1.opExtrude","CAP_EDGE",EDGE,{"disambiguationData":[OSD([sQuery(id+"F3.wireOp",EDGE,"E119")])],"isStart":false});
            var Q17;
            Q17=makeQuery(id+"F1.opExtrude","CAP_EDGE",EDGE,{"disambiguationData":[OSD([sQuery(id+"F3.wireOp",EDGE,"E3")])],"isStart":false});
            var Q18;
            Q18=makeQuery(id+"F0.opExtrude","CAP_EDGE",EDGE,{"disambiguationData":[OSD([sQuery(id+"F3.wireOp",EDGE,"E76")])],"isStart":false});
            var Q19;
            Q19=makeQuery(id+"F0.opExtrude","CAP_EDGE",EDGE,{"disambiguationData":[OSD([sQuery(id+"F3.wireOp",EDGE,"E77")])],"isStart":false});
            var Q20;
            Q20=makeQuery(id+"F0.opExtrude","CAP_FACE",FACE,{"disambiguationData":[OSD([sQuery(id+"F3.wireOp",EDGE,"E1"),sQuery(id+"F3.wireOp",EDGE,"E2"),sQuery(id+"F3.wireOp",EDGE,"E3"),sQuery(id+"F3.wireOp",EDGE,"E4"),sQuery(id+"F3.wireOp",EDGE,"E5"),sQuery(id+"F3.wireOp",EDGE,"E6"),sQuery(id+"F3.wireOp",EDGE,"E7"),sQuery(id+"F3.wireOp",EDGE,"E8"),sQuery(id+"F3.wireOp",EDGE,"E9"),sQuery(id+"F3.wireOp",EDGE,"E10"),sQuery(id+"F3.wireOp",EDGE,"E11"),sQuery(id+"F3.wireOp",EDGE,"E12"),sQuery(id+"F3.wireOp",EDGE,"E13"),sQuery(id+"F3.wireOp",EDGE,"E14"),sQuery(id+"F3.wireOp",EDGE,"E15"),sQuery(id+"F3.wireOp",EDGE,"E16"),sQuery(id+"F3.wireOp",EDGE,"E17"),sQuery(id+"F3.wireOp",EDGE,"E18"),sQuery(id+"F3.wireOp",EDGE,"E19"),sQuery(id+"F3.wireOp",EDGE,"E20"),sQuery(id+"F3.wireOp",EDGE,"E21"),sQuery(id+"F3.wireOp",EDGE,"E22"),sQuery(id+"F3.wireOp",EDGE,"E23"),sQuery(id+"F3.wireOp",EDGE,"E24"),sQuery(id+"F3.wireOp",EDGE,"E25"),sQuery(id+"F3.wireOp",EDGE,"E26"),sQuery(id+"F3.wireOp",EDGE,"E27"),sQuery(id+"F3.wireOp",EDGE,"E28"),sQuery(id+"F3.wireOp",EDGE,"E29"),sQuery(id+"F3.wireOp",EDGE,"E30"),sQuery(id+"F3.wireOp",EDGE,"E31"),sQuery(id+"F3.wireOp",EDGE,"E32"),sQuery(id+"F3.wireOp",EDGE,"E33"),sQuery(id+"F3.wireOp",EDGE,"E34"),sQuery(id+"F3.wireOp",EDGE,"E35"),sQuery(id+"F3.wireOp",EDGE,"E36"),sQuery(id+"F3.wireOp",EDGE,"E37"),sQuery(id+"F3.wireOp",EDGE,"E38"),sQuery(id+"F3.wireOp",EDGE,"E39"),sQuery(id+"F3.wireOp",EDGE,"E40"),sQuery(id+"F3.wireOp",EDGE,"E41"),sQuery(id+"F3.wireOp",EDGE,"E42"),sQuery(id+"F3.wireOp",EDGE,"E43"),sQuery(id+"F3.wireOp",EDGE,"E44"),sQuery(id+"F3.wireOp",EDGE,"E45"),sQuery(id+"F3.wireOp",EDGE,"E46"),sQuery(id+"F3.wireOp",EDGE,"E47"),sQuery(id+"F3.wireOp",EDGE,"E48"),sQuery(id+"F3.wireOp",EDGE,"E50"),sQuery(id+"F3.wireOp",EDGE,"E51"),sQuery(id+"F3.wireOp",EDGE,"E52"),sQuery(id+"F3.wireOp",EDGE,"E53"),sQuery(id+"F3.wireOp",EDGE,"E54"),sQuery(id+"F3.wireOp",EDGE,"E55"),sQuery(id+"F3.wireOp",EDGE,"E56"),sQuery(id+"F3.wireOp",EDGE,"E57"),sQuery(id+"F3.wireOp",EDGE,"E58"),sQuery(id+"F3.wireOp",EDGE,"E59"),sQuery(id+"F3.wireOp",EDGE,"E61"),sQuery(id+"F3.wireOp",EDGE,"E62"),sQuery(id+"F3.wireOp",EDGE,"E63"),sQuery(id+"F3.wireOp",EDGE,"E64"),sQuery(id+"F3.wireOp",EDGE,"E65"),sQuery(id+"F3.wireOp",EDGE,"E66"),sQuery(id+"F3.wireOp",EDGE,"E67"),sQuery(id+"F3.wireOp",EDGE,"E68"),sQuery(id+"F3.wireOp",EDGE,"E69"),sQuery(id+"F3.wireOp",EDGE,"E70"),sQuery(id+"F3.wireOp",EDGE,"E71"),sQuery(id+"F3.wireOp",EDGE,"E73"),sQuery(id+"F3.wireOp",EDGE,"E74"),sQuery(id+"F3.wireOp",EDGE,"E75"),sQuery(id+"F3.wireOp",EDGE,"E76"),sQuery(id+"F3.wireOp",EDGE,"E77")])],"isStart":false});
            var Q21;
            Q21=makeQuery(id+"F1.opExtrude","CAP_EDGE",EDGE,{"disambiguationData":[OSD([sQuery(id+"F3.wireOp",EDGE,"E11")])],"isStart":false});
            var Q22;
            Q22=makeQuery(id+"F1.opExtrude","CAP_EDGE",EDGE,{"disambiguationData":[OSD([sQuery(id+"F3.wireOp",EDGE,"E109")])],"isStart":false});
            var Q23;
            Q23=makeQuery(id+"F1.opExtrude","CAP_EDGE",EDGE,{"disambiguationData":[OSD([sQuery(id+"F3.wireOp",EDGE,"E9")])],"isStart":false});
            var Q24;
            Q24=makeQuery(id+"F1.opExtrude","CAP_EDGE",EDGE,{"disambiguationData":[OSD([sQuery(id+"F3.wireOp",EDGE,"E118")])],"isStart":false});
            var Q25;
            Q25=makeQuery(id+"F1.opExtrude","CAP_EDGE",EDGE,{"disambiguationData":[OSD([sQuery(id+"F3.wireOp",EDGE,"E12")])],"isStart":false});
            var Q26;
            Q26=makeQuery(id+"F1.opExtrude","CAP_EDGE",EDGE,{"disambiguationData":[OSD([sQuery(id+"F3.wireOp",EDGE,"E117")])],"isStart":false});
            var Q27;
            Q27=makeQuery(id+"F1.opExtrude","CAP_EDGE",EDGE,{"disambiguationData":[OSD([sQuery(id+"F3.wireOp",EDGE,"E10")])],"isStart":false});
            var Q28;
            Q28=makeQuery(id+"F1.opExtrude","CAP_EDGE",EDGE,{"disambiguationData":[OSD([sQuery(id+"F3.wireOp",EDGE,"E129")])],"isStart":false});
            var Q29;
            Q29=makeQuery(id+"F1.opExtrude","CAP_EDGE",EDGE,{"disambiguationData":[OSD([sQuery(id+"F3.wireOp",EDGE,"E6")])],"isStart":false});
            var Q30;
            Q30=makeQuery(id+"F1.opExtrude","CAP_EDGE",EDGE,{"disambiguationData":[OSD([sQuery(id+"F3.wireOp",EDGE,"E126")])],"isStart":false});
            var Q31;
            Q31=makeQuery(id+"F1.opExtrude","CAP_EDGE",EDGE,{"disambiguationData":[OSD([sQuery(id+"F3.wireOp",EDGE,"E13")])],"isStart":false});
            var Q32;
            Q32=makeQuery(id+"F1.opExtrude","CAP_EDGE",EDGE,{"disambiguationData":[OSD([sQuery(id+"F3.wireOp",EDGE,"E115")])],"isStart":false});
            var Q33;
            Q33=makeQuery(id+"F1.opExtrude","CAP_EDGE",EDGE,{"disambiguationData":[OSD([sQuery(id+"F3.wireOp",EDGE,"E17")])],"isStart":false});
            var Q34;
            Q34=makeQuery(id+"F1.opExtrude","CAP_EDGE",EDGE,{"disambiguationData":[OSD([sQuery(id+"F3.wireOp",EDGE,"E111")])],"isStart":false});
            var Q35;
            Q35=makeQuery(id+"F1.opExtrude","CAP_EDGE",EDGE,{"disambiguationData":[OSD([sQuery(id+"F3.wireOp",EDGE,"E14")])],"isStart":false});
            var Q36;
            Q36=makeQuery(id+"F1.opExtrude","CAP_EDGE",EDGE,{"disambiguationData":[OSD([sQuery(id+"F3.wireOp",EDGE,"E110")])],"isStart":false});
            var Q37;
            Q37=makeQuery(id+"F1.opExtrude","CAP_EDGE",EDGE,{"disambiguationData":[OSD([sQuery(id+"F3.wireOp",EDGE,"E18")])],"isStart":false});
            var Q38;
            Q38=makeQuery(id+"F1.opExtrude","CAP_EDGE",EDGE,{"disambiguationData":[OSD([sQuery(id+"F3.wireOp",EDGE,"E114")])],"isStart":false});
            var Q39;
            Q39=makeQuery(id+"F1.opExtrude","CAP_EDGE",EDGE,{"disambiguationData":[OSD([sQuery(id+"F3.wireOp",EDGE,"E15")])],"isStart":false});
            var Q40;
            Q40=makeQuery(id+"F1.opExtrude","CAP_EDGE",EDGE,{"disambiguationData":[OSD([sQuery(id+"F3.wireOp",EDGE,"E116")])],"isStart":false});
            var Q41;
            Q41=makeQuery(id+"F1.opExtrude","CAP_EDGE",EDGE,{"disambiguationData":[OSD([sQuery(id+"F3.wireOp",EDGE,"E20")])],"isStart":false});
            var Q42;
            Q42=makeQuery(id+"F1.opExtrude","CAP_EDGE",EDGE,{"disambiguationData":[OSD([sQuery(id+"F3.wireOp",EDGE,"E112")])],"isStart":false});
            var Q43;
            Q43=makeQuery(id+"F1.opExtrude","CAP_EDGE",EDGE,{"disambiguationData":[OSD([sQuery(id+"F3.wireOp",EDGE,"E22")])],"isStart":false});
            var Q44;
            Q44=makeQuery(id+"F1.opExtrude","CAP_EDGE",EDGE,{"disambiguationData":[OSD([sQuery(id+"F3.wireOp",EDGE,"E113")])],"isStart":false});
            var Q45;
            Q45=makeQuery(id+"F1.opExtrude","CAP_EDGE",EDGE,{"disambiguationData":[OSD([sQuery(id+"F3.wireOp",EDGE,"E28")])],"isStart":false});
            var Q46;
            Q46=makeQuery(id+"F1.opExtrude","CAP_EDGE",EDGE,{"disambiguationData":[OSD([sQuery(id+"F3.wireOp",EDGE,"E101")])],"isStart":false});
            var Q47;
            Q47=makeQuery(id+"F1.opExtrude","CAP_EDGE",EDGE,{"disambiguationData":[OSD([sQuery(id+"F3.wireOp",EDGE,"E25")])],"isStart":false});
            var Q48;
            Q48=makeQuery(id+"F1.opExtrude","CAP_EDGE",EDGE,{"disambiguationData":[OSD([sQuery(id+"F3.wireOp",EDGE,"E104")])],"isStart":false});
            var Q49;
            Q49=makeQuery(id+"F1.opExtrude","CAP_EDGE",EDGE,{"disambiguationData":[OSD([sQuery(id+"F3.wireOp",EDGE,"E23")])],"isStart":false});
            var Q50;
            Q50=makeQuery(id+"F1.opExtrude","CAP_EDGE",EDGE,{"disambiguationData":[OSD([sQuery(id+"F3.wireOp",EDGE,"E105")])],"isStart":false});
            var Q51;
            Q51=makeQuery(id+"F1.opExtrude","CAP_EDGE",EDGE,{"disambiguationData":[OSD([sQuery(id+"F3.wireOp",EDGE,"E19")])],"isStart":false});
            var Q52;
            Q52=makeQuery(id+"F1.opExtrude","CAP_EDGE",EDGE,{"disambiguationData":[OSD([sQuery(id+"F3.wireOp",EDGE,"E108")])],"isStart":false});
            var Q53;
            Q53=makeQuery(id+"F1.opExtrude","CAP_EDGE",EDGE,{"disambiguationData":[OSD([sQuery(id+"F3.wireOp",EDGE,"E16")])],"isStart":false});
            var Q54;
            Q54=makeQuery(id+"F1.opExtrude","CAP_EDGE",EDGE,{"disambiguationData":[OSD([sQuery(id+"F3.wireOp",EDGE,"E106")])],"isStart":false});
            var Q55;
            Q55=makeQuery(id+"F1.opExtrude","CAP_EDGE",EDGE,{"disambiguationData":[OSD([sQuery(id+"F3.wireOp",EDGE,"E21")])],"isStart":false});
            var Q56;
            Q56=makeQuery(id+"F1.opExtrude","CAP_EDGE",EDGE,{"disambiguationData":[OSD([sQuery(id+"F3.wireOp",EDGE,"E107")])],"isStart":false});
            var Q57;
            Q57=makeQuery(id+"F1.opExtrude","CAP_EDGE",EDGE,{"disambiguationData":[OSD([sQuery(id+"F3.wireOp",EDGE,"E24")])],"isStart":false});
            var Q58;
            Q58=makeQuery(id+"F1.opExtrude","CAP_EDGE",EDGE,{"disambiguationData":[OSD([sQuery(id+"F3.wireOp",EDGE,"E102")])],"isStart":false});
            var Q59;
            Q59=makeQuery(id+"F1.opExtrude","CAP_EDGE",EDGE,{"disambiguationData":[OSD([sQuery(id+"F3.wireOp",EDGE,"E27")])],"isStart":false});
            var Q60;
            Q60=makeQuery(id+"F1.opExtrude","CAP_EDGE",EDGE,{"disambiguationData":[OSD([sQuery(id+"F3.wireOp",EDGE,"E103")])],"isStart":false});
            var Q61;
            Q61=makeQuery(id+"F1.opExtrude","CAP_EDGE",EDGE,{"disambiguationData":[OSD([sQuery(id+"F3.wireOp",EDGE,"E32")])],"isStart":false});
            var Q62;
            Q62=makeQuery(id+"F1.opExtrude","CAP_EDGE",EDGE,{"disambiguationData":[OSD([sQuery(id+"F3.wireOp",EDGE,"E100")])],"isStart":false});
            var Q63;
            Q63=makeQuery(id+"F1.opExtrude","CAP_EDGE",EDGE,{"disambiguationData":[OSD([sQuery(id+"F3.wireOp",EDGE,"E26")])],"isStart":false});
            var Q64;
            Q64=makeQuery(id+"F1.opExtrude","CAP_EDGE",EDGE,{"disambiguationData":[OSD([sQuery(id+"F3.wireOp",EDGE,"E92")])],"isStart":false});
            var Q65;
            Q65=makeQuery(id+"F1.opExtrude","CAP_EDGE",EDGE,{"disambiguationData":[OSD([sQuery(id+"F3.wireOp",EDGE,"E29")])],"isStart":false});
            var Q66;
            Q66=makeQuery(id+"F1.opExtrude","CAP_EDGE",EDGE,{"disambiguationData":[OSD([sQuery(id+"F3.wireOp",EDGE,"E93")])],"isStart":false});
            var Q67;
            Q67=makeQuery(id+"F1.opExtrude","CAP_EDGE",EDGE,{"disambiguationData":[OSD([sQuery(id+"F3.wireOp",EDGE,"E31")])],"isStart":false});
            var Q68;
            Q68=makeQuery(id+"F1.opExtrude","CAP_EDGE",EDGE,{"disambiguationData":[OSD([sQuery(id+"F3.wireOp",EDGE,"E94")])],"isStart":false});
            var Q69;
            Q69=makeQuery(id+"F1.opExtrude","CAP_EDGE",EDGE,{"disambiguationData":[OSD([sQuery(id+"F3.wireOp",EDGE,"E34")])],"isStart":false});
            var Q70;
            Q70=makeQuery(id+"F1.opExtrude","CAP_EDGE",EDGE,{"disambiguationData":[OSD([sQuery(id+"F3.wireOp",EDGE,"E97")])],"isStart":false});
            var Q71;
            Q71=makeQuery(id+"F1.opExtrude","CAP_EDGE",EDGE,{"disambiguationData":[OSD([sQuery(id+"F3.wireOp",EDGE,"E33")])],"isStart":false});
            var Q72;
            Q72=makeQuery(id+"F1.opExtrude","CAP_EDGE",EDGE,{"disambiguationData":[OSD([sQuery(id+"F3.wireOp",EDGE,"E99")])],"isStart":false});
            var Q73;
            Q73=makeQuery(id+"F1.opExtrude","CAP_EDGE",EDGE,{"disambiguationData":[OSD([sQuery(id+"F3.wireOp",EDGE,"E30")])],"isStart":false});
            var Q74;
            Q74=makeQuery(id+"F1.opExtrude","CAP_EDGE",EDGE,{"disambiguationData":[OSD([sQuery(id+"F3.wireOp",EDGE,"E91")])],"isStart":false});
            var Q75;
            Q75=makeQuery(id+"F1.opExtrude","CAP_EDGE",EDGE,{"disambiguationData":[OSD([sQuery(id+"F3.wireOp",EDGE,"E37")])],"isStart":false});
            var Q76;
            Q76=makeQuery(id+"F1.opExtrude","CAP_EDGE",EDGE,{"disambiguationData":[OSD([sQuery(id+"F3.wireOp",EDGE,"E90")])],"isStart":false});
            var Q77;
            Q77=makeQuery(id+"F1.opExtrude","CAP_EDGE",EDGE,{"disambiguationData":[OSD([sQuery(id+"F3.wireOp",EDGE,"E38")])],"isStart":false});
            var Q78;
            Q78=makeQuery(id+"F1.opExtrude","CAP_EDGE",EDGE,{"disambiguationData":[OSD([sQuery(id+"F3.wireOp",EDGE,"E89")])],"isStart":false});
            var Q79;
            Q79=makeQuery(id+"F1.opExtrude","CAP_EDGE",EDGE,{"disambiguationData":[OSD([sQuery(id+"F3.wireOp",EDGE,"E39")])],"isStart":false});
            var Q80;
            Q80=makeQuery(id+"F1.opExtrude","CAP_EDGE",EDGE,{"disambiguationData":[OSD([sQuery(id+"F3.wireOp",EDGE,"E88")])],"isStart":false});
            var Q81;
            Q81=makeQuery(id+"F1.opExtrude","CAP_EDGE",EDGE,{"disambiguationData":[OSD([sQuery(id+"F3.wireOp",EDGE,"E36")])],"isStart":false});
            var Q82;
            Q82=makeQuery(id+"F1.opExtrude","CAP_EDGE",EDGE,{"disambiguationData":[OSD([sQuery(id+"F3.wireOp",EDGE,"E95")])],"isStart":false});
            var Q83;
            Q83=makeQuery(id+"F0.opExtrude","CAP_EDGE",EDGE,{"disambiguationData":[OSD([sQuery(id+"F3.wireOp",EDGE,"E40")])],"isStart":false});
            var Q84;
            Q84=makeQuery(id+"F1.opExtrude","CAP_EDGE",EDGE,{"disambiguationData":[OSD([sQuery(id+"F3.wireOp",EDGE,"E96")])],"isStart":false});
            var Q85;
            Q85=makeQuery(id+"F1.opExtrude","CAP_EDGE",EDGE,{"disambiguationData":[OSD([sQuery(id+"F3.wireOp",EDGE,"E35")])],"isStart":false});
            var Q86;
            Q86=makeQuery(id+"F1.opExtrude","CAP_EDGE",EDGE,{"disambiguationData":[OSD([sQuery(id+"F3.wireOp",EDGE,"E98")])],"isStart":false});
            var Q87;
            Q87=makeQuery(id+"F1.opExtrude","CAP_EDGE",EDGE,{"disambiguationData":[OSD([sQuery(id+"F3.wireOp",EDGE,"E41")])],"isStart":false});
            var Q88;
            Q88=makeQuery(id+"F1.opExtrude","CAP_EDGE",EDGE,{"disambiguationData":[OSD([sQuery(id+"F3.wireOp",EDGE,"E86")])],"isStart":false});
            var Q89;
            Q89=makeQuery(id+"F1.opExtrude","CAP_EDGE",EDGE,{"disambiguationData":[OSD([sQuery(id+"F3.wireOp",EDGE,"E42")])],"isStart":false});
            var Q90;
            Q90=makeQuery(id+"F1.opExtrude","CAP_EDGE",EDGE,{"disambiguationData":[OSD([sQuery(id+"F3.wireOp",EDGE,"E87")])],"isStart":false});
            var Q91;
            Q91=makeQuery(id+"F1.opExtrude","CAP_EDGE",EDGE,{"disambiguationData":[OSD([sQuery(id+"F3.wireOp",EDGE,"E44")])],"isStart":false});
            var Q92;
            Q92=makeQuery(id+"F1.opExtrude","CAP_EDGE",EDGE,{"disambiguationData":[OSD([sQuery(id+"F3.wireOp",EDGE,"E82")])],"isStart":false});
            var Q93;
            Q93=makeQuery(id+"F1.opExtrude","CAP_EDGE",EDGE,{"disambiguationData":[OSD([sQuery(id+"F3.wireOp",EDGE,"E48")])],"isStart":false});
            var Q94;
            Q94=makeQuery(id+"F1.opExtrude","CAP_EDGE",EDGE,{"disambiguationData":[OSD([sQuery(id+"F3.wireOp",EDGE,"E84")])],"isStart":false});
            var Q95;
            Q95=makeQuery(id+"F1.opExtrude","CAP_EDGE",EDGE,{"disambiguationData":[OSD([sQuery(id+"F3.wireOp",EDGE,"E74")])],"isStart":false});
            var Q96;
            Q96=makeQuery(id+"F1.opExtrude","CAP_EDGE",EDGE,{"disambiguationData":[OSD([sQuery(id+"F3.wireOp",EDGE,"E81")])],"isStart":false});
            var Q97;
            Q97=makeQuery(id+"F1.opExtrude","CAP_EDGE",EDGE,{"disambiguationData":[OSD([sQuery(id+"F3.wireOp",EDGE,"E45")])],"isStart":false});
            var Q98;
            Q98=makeQuery(id+"F1.opExtrude","CAP_EDGE",EDGE,{"disambiguationData":[OSD([sQuery(id+"F3.wireOp",EDGE,"E85")])],"isStart":false});
            var Q99;
            Q99=makeQuery(id+"F1.opExtrude","CAP_EDGE",EDGE,{"disambiguationData":[OSD([sQuery(id+"F3.wireOp",EDGE,"E47")])],"isStart":false});
            var Q100;
            Q100=makeQuery(id+"F1.opExtrude","CAP_EDGE",EDGE,{"disambiguationData":[OSD([sQuery(id+"F3.wireOp",EDGE,"E80")])],"isStart":false});
            var Q101;
            Q101=makeQuery(id+"F1.opExtrude","CAP_EDGE",EDGE,{"disambiguationData":[OSD([sQuery(id+"F3.wireOp",EDGE,"E73")])],"isStart":false});
            var Q102;
            Q102=makeQuery(id+"F1.opExtrude","CAP_EDGE",EDGE,{"disambiguationData":[OSD([sQuery(id+"F3.wireOp",EDGE,"E79")])],"isStart":false});
            var Q103;
            Q103=makeQuery(id+"F1.opExtrude","CAP_EDGE",EDGE,{"disambiguationData":[OSD([sQuery(id+"F3.wireOp",EDGE,"E43")])],"isStart":false});
            var Q104;
            Q104=makeQuery(id+"F1.opExtrude","CAP_EDGE",EDGE,{"disambiguationData":[OSD([sQuery(id+"F3.wireOp",EDGE,"E83")])],"isStart":false});
            var Q105;
            Q105=makeQuery(id+"F1.opExtrude","CAP_EDGE",EDGE,{"disambiguationData":[OSD([sQuery(id+"F3.wireOp",EDGE,"E46")])],"isStart":false});
            var Q106;
            Q106=makeQuery(id+"F1.opExtrude","CAP_EDGE",EDGE,{"disambiguationData":[OSD([sQuery(id+"F3.wireOp",EDGE,"E78")])],"isStart":false});
            var Q107;
            {var subQ0=sQuery(id+"F3.wireOp",EDGE,"E77");var subQ1=sQuery(id+"F3.wireOp",EDGE,"E76");var subQ2=sQuery(id+"F3.wireOp",EDGE,"E74");var subQ3=sQuery(id+"F3.wireOp",EDGE,"E73");var subQ4=sQuery(id+"F3.wireOp",EDGE,"E48");var subQ5=sQuery(id+"F3.wireOp",EDGE,"E47");var subQ6=sQuery(id+"F3.wireOp",EDGE,"E46");var subQ7=sQuery(id+"F3.wireOp",EDGE,"E45");var subQ8=sQuery(id+"F3.wireOp",EDGE,"E44");var subQ9=sQuery(id+"F3.wireOp",EDGE,"E43");var subQ10=sQuery(id+"F3.wireOp",EDGE,"E42");var subQ11=sQuery(id+"F3.wireOp",EDGE,"E41");var subQ12=sQuery(id+"F3.wireOp",EDGE,"E40");var subQ13=sQuery(id+"F3.wireOp",EDGE,"E39");var subQ14=sQuery(id+"F3.wireOp",EDGE,"E38");var subQ15=sQuery(id+"F3.wireOp",EDGE,"E37");var subQ16=sQuery(id+"F3.wireOp",EDGE,"E36");var subQ17=sQuery(id+"F3.wireOp",EDGE,"E35");var subQ18=sQuery(id+"F3.wireOp",EDGE,"E34");var subQ19=sQuery(id+"F3.wireOp",EDGE,"E33");var subQ20=sQuery(id+"F3.wireOp",EDGE,"E32");var subQ21=sQuery(id+"F3.wireOp",EDGE,"E31");var subQ22=sQuery(id+"F3.wireOp",EDGE,"E30");var subQ23=sQuery(id+"F3.wireOp",EDGE,"E29");var subQ24=sQuery(id+"F3.wireOp",EDGE,"E28");var subQ25=sQuery(id+"F3.wireOp",EDGE,"E27");var subQ26=sQuery(id+"F3.wireOp",EDGE,"E26");var subQ27=sQuery(id+"F3.wireOp",EDGE,"E25");var subQ28=sQuery(id+"F3.wireOp",EDGE,"E24");var subQ29=sQuery(id+"F3.wireOp",EDGE,"E23");var subQ30=sQuery(id+"F3.wireOp",EDGE,"E22");var subQ31=sQuery(id+"F3.wireOp",EDGE,"E21");var subQ32=sQuery(id+"F3.wireOp",EDGE,"E20");var subQ33=sQuery(id+"F3.wireOp",EDGE,"E19");var subQ34=sQuery(id+"F3.wireOp",EDGE,"E18");var subQ35=sQuery(id+"F3.wireOp",EDGE,"E17");var subQ36=sQuery(id+"F3.wireOp",EDGE,"E16");var subQ37=sQuery(id+"F3.wireOp",EDGE,"E15");var subQ38=sQuery(id+"F3.wireOp",EDGE,"E14");var subQ39=sQuery(id+"F3.wireOp",EDGE,"E13");var subQ40=sQuery(id+"F3.wireOp",EDGE,"E12");var subQ41=sQuery(id+"F3.wireOp",EDGE,"E11");var subQ42=sQuery(id+"F3.wireOp",EDGE,"E10");var subQ43=sQuery(id+"F3.wireOp",EDGE,"E9");var subQ44=sQuery(id+"F3.wireOp",EDGE,"E8");var subQ45=sQuery(id+"F3.wireOp",EDGE,"E7");var subQ46=sQuery(id+"F3.wireOp",EDGE,"E6");var subQ47=sQuery(id+"F3.wireOp",EDGE,"E5");var subQ48=sQuery(id+"F3.wireOp",EDGE,"E4");var subQ49=sQuery(id+"F3.wireOp",EDGE,"E3");var subQ50=sQuery(id+"F3.wireOp",EDGE,"E2");var subQ51=sQuery(id+"F3.wireOp",EDGE,"E1");Q107=makeQuery(id+"F1.boolean.opBoolean","MERGE",FACE,{"derivedFrom":[makeQuery(id+"F0.opExtrude","CAP_FACE",FACE,{"disambiguationData":[OSD([subQ51,subQ50,subQ49,subQ48,subQ47,subQ46,subQ45,subQ44,subQ43,subQ42,subQ41,subQ40,subQ39,subQ38,subQ37,subQ36,subQ35,subQ34,subQ33,subQ32,subQ31,subQ30,subQ29,subQ28,subQ27,subQ26,subQ25,subQ24,subQ23,subQ22,subQ21,subQ20,subQ19,subQ18,subQ17,subQ16,subQ15,subQ14,subQ13,subQ12,subQ11,subQ10,subQ9,subQ8,subQ7,subQ6,subQ5,subQ4,sQuery(id+"F3.wireOp",EDGE,"E50"),sQuery(id+"F3.wireOp",EDGE,"E51"),sQuery(id+"F3.wireOp",EDGE,"E52"),sQuery(id+"F3.wireOp",EDGE,"E53"),sQuery(id+"F3.wireOp",EDGE,"E54"),sQuery(id+"F3.wireOp",EDGE,"E55"),sQuery(id+"F3.wireOp",EDGE,"E56"),sQuery(id+"F3.wireOp",EDGE,"E57"),sQuery(id+"F3.wireOp",EDGE,"E58"),sQuery(id+"F3.wireOp",EDGE,"E59"),sQuery(id+"F3.wireOp",EDGE,"E61"),sQuery(id+"F3.wireOp",EDGE,"E62"),sQuery(id+"F3.wireOp",EDGE,"E63"),sQuery(id+"F3.wireOp",EDGE,"E64"),sQuery(id+"F3.wireOp",EDGE,"E65"),sQuery(id+"F3.wireOp",EDGE,"E66"),sQuery(id+"F3.wireOp",EDGE,"E67"),sQuery(id+"F3.wireOp",EDGE,"E68"),sQuery(id+"F3.wireOp",EDGE,"E69"),sQuery(id+"F3.wireOp",EDGE,"E70"),sQuery(id+"F3.wireOp",EDGE,"E71"),subQ3,subQ2,sQuery(id+"F3.wireOp",EDGE,"E75"),subQ1,subQ0])],"isStart":true}),makeQuery(id+"F1.opExtrude","CAP_FACE",FACE,{"disambiguationData":[OSD([subQ51,sQuery(id+"F3.wireOp",EDGE,"E121")])],"isStart":true}),makeQuery(id+"F1.opExtrude","CAP_FACE",FACE,{"disambiguationData":[OSD([subQ50,sQuery(id+"F3.wireOp",EDGE,"E120")])],"isStart":true}),makeQuery(id+"F1.opExtrude","CAP_FACE",FACE,{"disambiguationData":[OSD([subQ49,sQuery(id+"F3.wireOp",EDGE,"E119")])],"isStart":true}),makeQuery(id+"F1.opExtrude","CAP_FACE",FACE,{"disambiguationData":[OSD([subQ48,sQuery(id+"F3.wireOp",EDGE,"E127")])],"isStart":true}),makeQuery(id+"F1.opExtrude","CAP_FACE",FACE,{"disambiguationData":[OSD([subQ47,sQuery(id+"F3.wireOp",EDGE,"E125")])],"isStart":true}),makeQuery(id+"F1.opExtrude","CAP_FACE",FACE,{"disambiguationData":[OSD([subQ46,sQuery(id+"F3.wireOp",EDGE,"E126")])],"isStart":true}),makeQuery(id+"F1.opExtrude","CAP_FACE",FACE,{"disambiguationData":[OSD([subQ45,sQuery(id+"F3.wireOp",EDGE,"E123")])],"isStart":true}),makeQuery(id+"F1.opExtrude","CAP_FACE",FACE,{"disambiguationData":[OSD([subQ44,sQuery(id+"F3.wireOp",EDGE,"E128")])],"isStart":true}),makeQuery(id+"F1.opExtrude","CAP_FACE",FACE,{"disambiguationData":[OSD([subQ43,sQuery(id+"F3.wireOp",EDGE,"E118")])],"isStart":true}),makeQuery(id+"F1.opExtrude","CAP_FACE",FACE,{"disambiguationData":[OSD([subQ42,sQuery(id+"F3.wireOp",EDGE,"E129")])],"isStart":true}),makeQuery(id+"F1.opExtrude","CAP_FACE",FACE,{"disambiguationData":[OSD([subQ41,sQuery(id+"F3.wireOp",EDGE,"E109")])],"isStart":true}),makeQuery(id+"F1.opExtrude","CAP_FACE",FACE,{"disambiguationData":[OSD([subQ40,sQuery(id+"F3.wireOp",EDGE,"E117")])],"isStart":true}),makeQuery(id+"F1.opExtrude","CAP_FACE",FACE,{"disambiguationData":[OSD([subQ39,sQuery(id+"F3.wireOp",EDGE,"E115")])],"isStart":true}),makeQuery(id+"F1.opExtrude","CAP_FACE",FACE,{"disambiguationData":[OSD([subQ38,sQuery(id+"F3.wireOp",EDGE,"E110")])],"isStart":true}),makeQuery(id+"F1.opExtrude","CAP_FACE",FACE,{"disambiguationData":[OSD([subQ37,sQuery(id+"F3.wireOp",EDGE,"E116")])],"isStart":true}),makeQuery(id+"F1.opExtrude","CAP_FACE",FACE,{"disambiguationData":[OSD([subQ36,sQuery(id+"F3.wireOp",EDGE,"E106")])],"isStart":true}),makeQuery(id+"F1.opExtrude","CAP_FACE",FACE,{"disambiguationData":[OSD([subQ35,sQuery(id+"F3.wireOp",EDGE,"E111")])],"isStart":true}),makeQuery(id+"F1.opExtrude","CAP_FACE",FACE,{"disambiguationData":[OSD([subQ34,sQuery(id+"F3.wireOp",EDGE,"E114")])],"isStart":true}),makeQuery(id+"F1.opExtrude","CAP_FACE",FACE,{"disambiguationData":[OSD([subQ33,sQuery(id+"F3.wireOp",EDGE,"E108")])],"isStart":true}),makeQuery(id+"F1.opExtrude","CAP_FACE",FACE,{"disambiguationData":[OSD([subQ32,sQuery(id+"F3.wireOp",EDGE,"E112")])],"isStart":true}),makeQuery(id+"F1.opExtrude","CAP_FACE",FACE,{"disambiguationData":[OSD([subQ31,sQuery(id+"F3.wireOp",EDGE,"E107")])],"isStart":true}),makeQuery(id+"F1.opExtrude","CAP_FACE",FACE,{"disambiguationData":[OSD([subQ30,sQuery(id+"F3.wireOp",EDGE,"E113")])],"isStart":true}),makeQuery(id+"F1.opExtrude","CAP_FACE",FACE,{"disambiguationData":[OSD([subQ29,sQuery(id+"F3.wireOp",EDGE,"E105")])],"isStart":true}),makeQuery(id+"F1.opExtrude","CAP_FACE",FACE,{"disambiguationData":[OSD([subQ28,sQuery(id+"F3.wireOp",EDGE,"E102")])],"isStart":true}),makeQuery(id+"F1.opExtrude","CAP_FACE",FACE,{"disambiguationData":[OSD([subQ27,sQuery(id+"F3.wireOp",EDGE,"E104")])],"isStart":true}),makeQuery(id+"F1.opExtrude","CAP_FACE",FACE,{"disambiguationData":[OSD([subQ26,sQuery(id+"F3.wireOp",EDGE,"E92")])],"isStart":true}),makeQuery(id+"F1.opExtrude","CAP_FACE",FACE,{"disambiguationData":[OSD([subQ25,sQuery(id+"F3.wireOp",EDGE,"E103")])],"isStart":true}),makeQuery(id+"F1.opExtrude","CAP_FACE",FACE,{"disambiguationData":[OSD([subQ24,sQuery(id+"F3.wireOp",EDGE,"E101")])],"isStart":true}),makeQuery(id+"F1.opExtrude","CAP_FACE",FACE,{"disambiguationData":[OSD([subQ23,sQuery(id+"F3.wireOp",EDGE,"E93")])],"isStart":true}),makeQuery(id+"F1.opExtrude","CAP_FACE",FACE,{"disambiguationData":[OSD([subQ22,sQuery(id+"F3.wireOp",EDGE,"E91")])],"isStart":true}),makeQuery(id+"F1.opExtrude","CAP_FACE",FACE,{"disambiguationData":[OSD([subQ21,sQuery(id+"F3.wireOp",EDGE,"E94")])],"isStart":true}),makeQuery(id+"F1.opExtrude","CAP_FACE",FACE,{"disambiguationData":[OSD([subQ20,sQuery(id+"F3.wireOp",EDGE,"E100")])],"isStart":true}),makeQuery(id+"F1.opExtrude","CAP_FACE",FACE,{"disambiguationData":[OSD([subQ19,sQuery(id+"F3.wireOp",EDGE,"E99")])],"isStart":true}),makeQuery(id+"F1.opExtrude","CAP_FACE",FACE,{"disambiguationData":[OSD([subQ18,sQuery(id+"F3.wireOp",EDGE,"E97")])],"isStart":true}),makeQuery(id+"F1.opExtrude","CAP_FACE",FACE,{"disambiguationData":[OSD([subQ17,sQuery(id+"F3.wireOp",EDGE,"E98")])],"isStart":true}),makeQuery(id+"F1.opExtrude","CAP_FACE",FACE,{"disambiguationData":[OSD([subQ16,sQuery(id+"F3.wireOp",EDGE,"E95")])],"isStart":true}),makeQuery(id+"F1.opExtrude","CAP_FACE",FACE,{"disambiguationData":[OSD([subQ15,sQuery(id+"F3.wireOp",EDGE,"E90")])],"isStart":true}),makeQuery(id+"F1.opExtrude","CAP_FACE",FACE,{"disambiguationData":[OSD([subQ14,sQuery(id+"F3.wireOp",EDGE,"E89")])],"isStart":true}),makeQuery(id+"F1.opExtrude","CAP_FACE",FACE,{"disambiguationData":[OSD([subQ13,sQuery(id+"F3.wireOp",EDGE,"E88")])],"isStart":true}),makeQuery(id+"F1.opExtrude","CAP_FACE",FACE,{"disambiguationData":[OSD([subQ12,sQuery(id+"F3.wireOp",EDGE,"E96")])],"isStart":true}),makeQuery(id+"F1.opExtrude","CAP_FACE",FACE,{"disambiguationData":[OSD([subQ11,sQuery(id+"F3.wireOp",EDGE,"E86")])],"isStart":true}),makeQuery(id+"F1.opExtrude","CAP_FACE",FACE,{"disambiguationData":[OSD([subQ10,sQuery(id+"F3.wireOp",EDGE,"E87")])],"isStart":true}),makeQuery(id+"F1.opExtrude","CAP_FACE",FACE,{"disambiguationData":[OSD([subQ9,sQuery(id+"F3.wireOp",EDGE,"E83")])],"isStart":true}),makeQuery(id+"F1.opExtrude","CAP_FACE",FACE,{"disambiguationData":[OSD([subQ8,sQuery(id+"F3.wireOp",EDGE,"E82")])],"isStart":true}),makeQuery(id+"F1.opExtrude","CAP_FACE",FACE,{"disambiguationData":[OSD([subQ7,sQuery(id+"F3.wireOp",EDGE,"E85")])],"isStart":true}),makeQuery(id+"F1.opExtrude","CAP_FACE",FACE,{"disambiguationData":[OSD([subQ6,sQuery(id+"F3.wireOp",EDGE,"E78")])],"isStart":true}),makeQuery(id+"F1.opExtrude","CAP_FACE",FACE,{"disambiguationData":[OSD([subQ5,sQuery(id+"F3.wireOp",EDGE,"E80")])],"isStart":true}),makeQuery(id+"F1.opExtrude","CAP_FACE",FACE,{"disambiguationData":[OSD([subQ4,sQuery(id+"F3.wireOp",EDGE,"E84")])],"isStart":true}),makeQuery(id+"F1.opExtrude","CAP_FACE",FACE,{"disambiguationData":[OSD([subQ3,sQuery(id+"F3.wireOp",EDGE,"E79")])],"isStart":true}),makeQuery(id+"F1.opExtrude","CAP_FACE",FACE,{"disambiguationData":[OSD([subQ2,sQuery(id+"F3.wireOp",EDGE,"E81")])],"isStart":true}),makeQuery(id+"F1.opExtrude","CAP_FACE",FACE,{"disambiguationData":[OSD([subQ1,sQuery(id+"F3.wireOp",EDGE,"E122")])],"isStart":true}),makeQuery(id+"F1.opExtrude","CAP_FACE",FACE,{"disambiguationData":[OSD([subQ0,sQuery(id+"F3.wireOp",EDGE,"E124")])],"isStart":true})]});}
            var Q108;
            Q108=makeQuery(id+"F1.opExtrude","CAP_EDGE",EDGE,{"disambiguationData":[OSD([sQuery(id+"F3.wireOp",EDGE,"E2")])],"isStart":false});
            fillet(context, id + "F2", {"entities" : qUnion([Q0, Q1, Q2, Q3, Q4, Q5, Q6, Q7, Q8, Q9, Q10, Q11, Q12, Q13, Q14, Q15, Q16, Q17, Q18, Q19, Q20, Q21, Q22, Q23, Q24, Q25, Q26, Q27, Q28, Q29, Q30, Q31, Q32, Q33, Q34, Q35, Q36, Q37, Q38, Q39, Q40, Q41, Q42, Q43, Q44, Q45, Q46, Q47, Q48, Q49, Q50, Q51, Q52, Q53, Q54, Q55, Q56, Q57, Q58, Q59, Q60, Q61, Q62, Q63, Q64, Q65, Q66, Q67, Q68, Q69, Q70, Q71, Q72, Q73, Q74, Q75, Q76, Q77, Q78, Q79, Q80, Q81, Q82, Q83, Q84, Q85, Q86, Q87, Q88, Q89, Q90, Q91, Q92, Q93, Q94, Q95, Q96, Q97, Q98, Q99, Q100, Q101, Q102, Q103, Q104, Q105, Q106, Q107, Q108]), "radius" : 0.5 * mm, "tangentPropagation" : true, "allowEdgeOverflow" : false});
        }
    });
